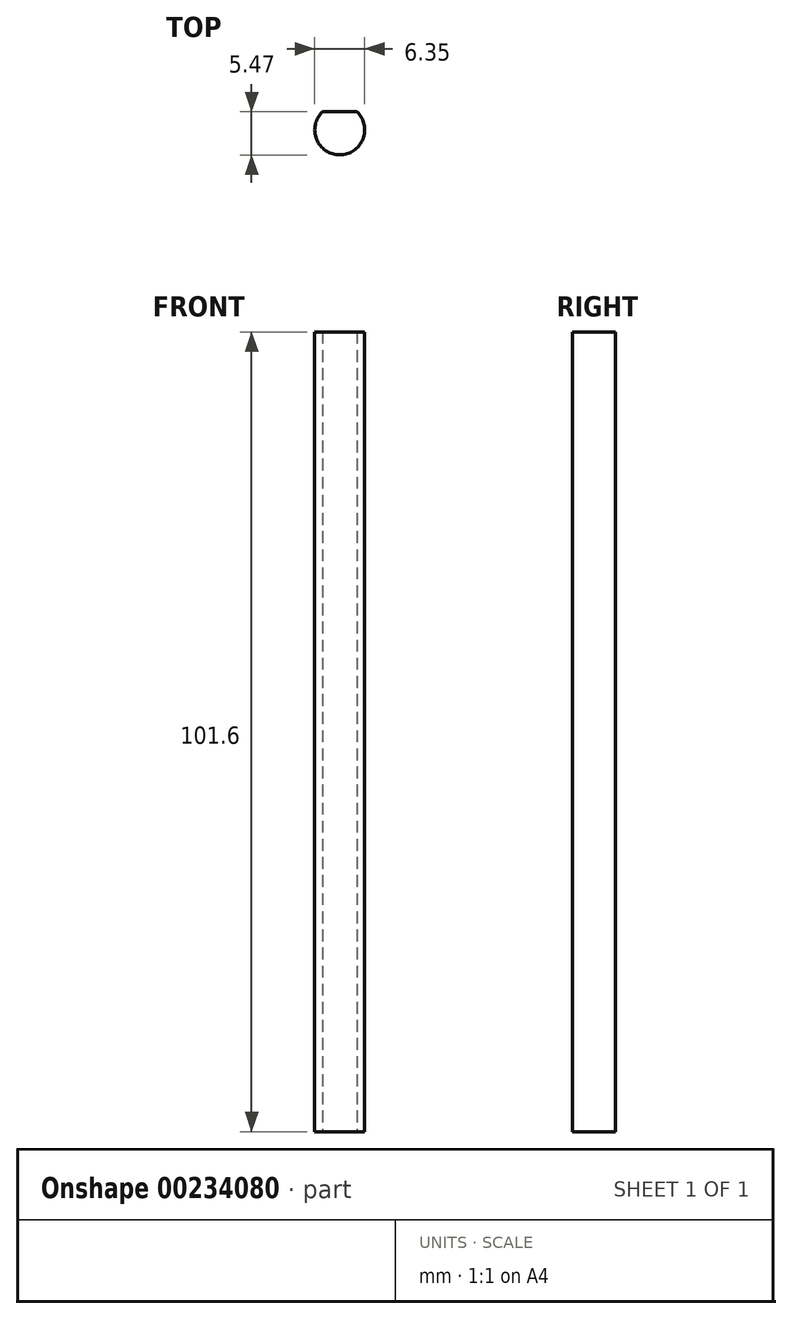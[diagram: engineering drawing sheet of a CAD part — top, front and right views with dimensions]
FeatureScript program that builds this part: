
annotation { "Feature Type Name" : "Feature", "Feature Type Description" : "" }
export const myFeature = defineFeature(function(context is Context, id is Id, definition is map)
    precondition{}
    {
        {
            var Q0;
            Q0=qCreatedBy(makeId("Top.planeOp"),FACE);
            var sketch = newSketch(context, id + "F0", { "sketchPlane" : qUnion([Q0])});
            skCircle(sketch, "E0", {"center": v(-116.19, -8.74) * mm, "radius": 3.18 * mm});
            skLineSegment(sketch, "E1", {"start": v(-118.38, -6.45) * mm, "end": v(-114, -6.45) * mm});
            skSolve(sketch);
        }
        {
            var Q0;
            {var subQ0=sQuery(id+"F0.wireOp",EDGE,"E1");Q0=makeQuery(id+"F0.imprint","IMPRINT",FACE,{"disambiguationData":[TD([[makeQuery(id+"F0.imprint","IMPRINT",EDGE,{"derivedFrom":subQ0}),-1.0]])]});}
            extrude(context, id + "F1", {"entities" : qUnion([Q0]), "depth" : 101.6 * mm});
        }
    });
